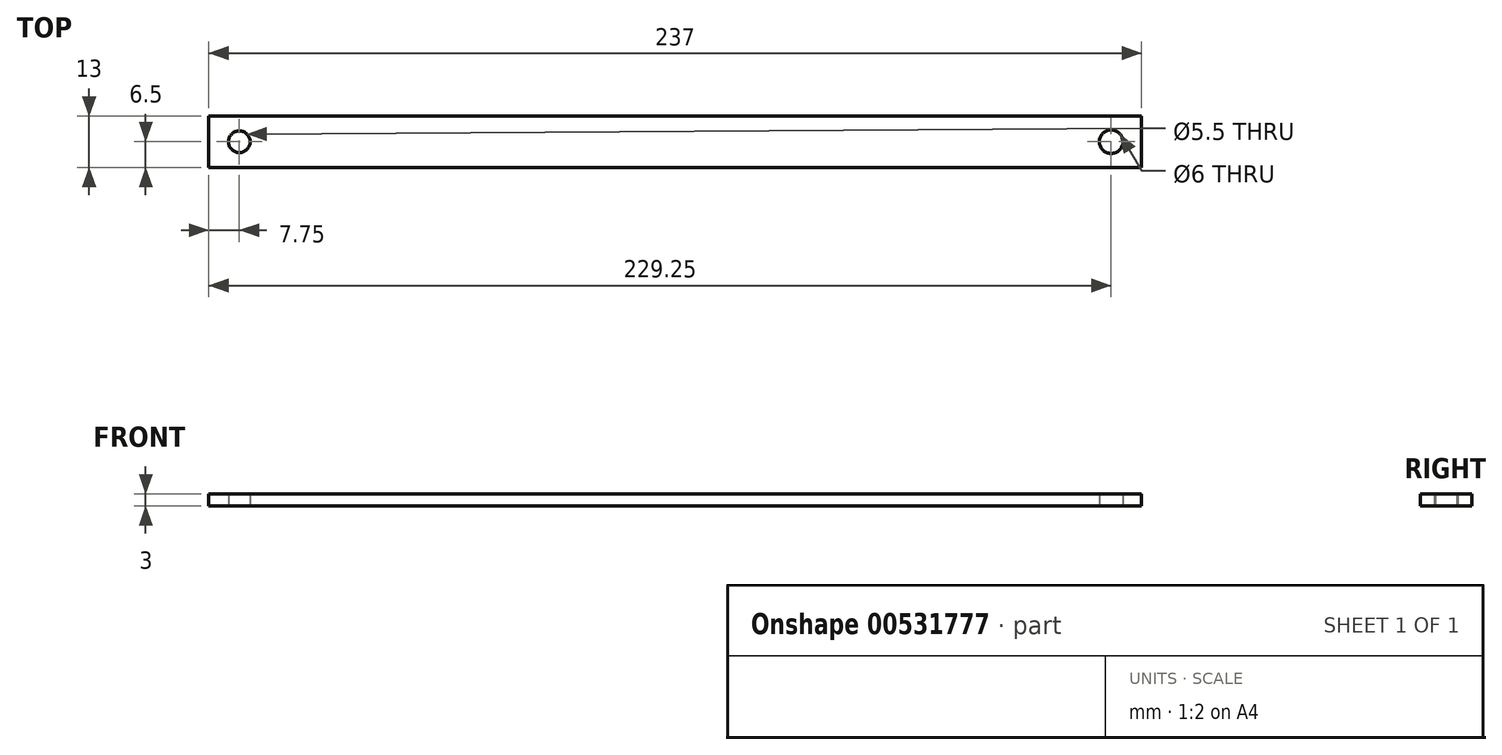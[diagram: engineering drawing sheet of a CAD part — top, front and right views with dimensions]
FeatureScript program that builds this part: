
annotation { "Feature Type Name" : "Feature", "Feature Type Description" : "" }
export const myFeature = defineFeature(function(context is Context, id is Id, definition is map)
    precondition{}
    {
        {
            var Q0;
            Q0=qCreatedBy(makeId("Top.planeOp"),FACE);
            var sketch = newSketch(context, id + "F0", { "sketchPlane" : qUnion([Q0])});
            skLineSegment(sketch, "E0.bottom", {"start": v(118.5, 6.5) * mm, "end": v(-118.5, 6.5) * mm});
            skLineSegment(sketch, "E0.top", {"start": v(118.5, -6.5) * mm, "end": v(-118.5, -6.5) * mm});
            skLineSegment(sketch, "E0.left", {"start": v(118.5, 6.5) * mm, "end": v(118.5, -6.5) * mm});
            skLineSegment(sketch, "E0.right", {"start": v(-118.5, 6.5) * mm, "end": v(-118.5, -6.5) * mm});
            skPoint(sketch, "E0.middle", {"position": v(0, 0) * mm});
            skCircle(sketch, "E1", {"center": v(-110.75, 0) * mm, "radius": 2.75 * mm});
            skCircle(sketch, "E2", {"center": v(110.75, 0) * mm, "radius": 3 * mm});
            skSolve(sketch);
        }
        {
            var Q0;
            Q0=makeQuery(id+"F0.imprint","IMPRINT",FACE,{"disambiguationData":[TD([[makeQuery(id+"F0.imprint","IMPRINT",EDGE,{"derivedFrom":sQuery(id+"F0.wireOp",EDGE,"E0.bottom")}),1.0]])]});
            extrude(context, id + "F1", {"entities" : qUnion([Q0]), "depth" : 3 * mm, "offsetDistance" : 25 * mm});
        }
    });
